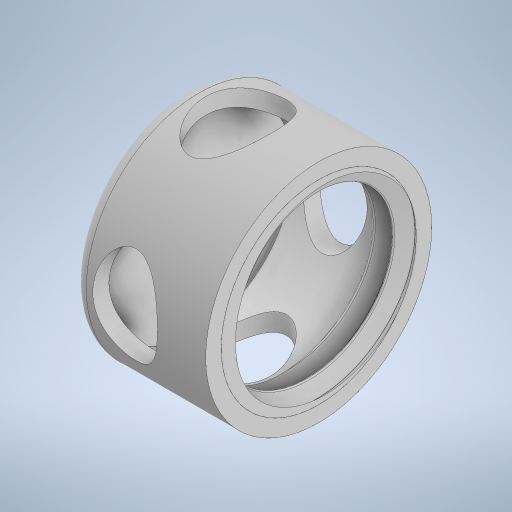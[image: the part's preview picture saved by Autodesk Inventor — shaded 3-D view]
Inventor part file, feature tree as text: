
AUTODESK INVENTOR PART (.ipt)
format: ipt  version: 2023 (Build 270158000, 158)  size: 494,080 bytes
history: native  units: in
note: dims shown in document units (in); Inventor stores cm internally (conversion verified against a paired STEP export)
features: sketch x6, extrude x5, fillet x1, thread x1, revolve x1, helix x1
ambient origin geometry x8: Origin, YZ Plane, XZ Plane, XY Plane, X Axis, Y Axis, Z Axis, Center Point
bodies: Solid1 (feature_tree), Solid11 (feature_tree)
feature tree (15):
  sketch  "Sketch1"  dims[d0=1.1811in d1=1.378in]
  extrude  "Extrusion2"  Depth=1.378in
  sketch  "Sketch2"  dims[d4=0.0591in d5=0.0in d6=0.1969in]
  sketch  "Sketch3"  dims[d7=0.2953in d8=0.315in]
  extrude  "Extrusion3"  Depth=0.1969in
  extrude  "Extrusion4"  Depth=0.315in
  extrude  "Extrusion5"  Depth=0.2953in
  fillet  "Fillet1"  Radius=0.315in
  extrude  "Extrusion7"  Depth=0.8071in TaperAngle=0.0deg
  thread  "Thread10"  [1 undecoded]
  revolve  "Revolution10"  [1 undecoded]
  helix  "Coil10"  [1 undecoded]
  sketch  "Sketch8"  dims[d9=0.1969in d10=0.2953in d11=0.315in]
  sketch  "Sketch23"  dims[d12=0.8071in d13=0.0in d14=1.5748in d15=0.0in d16=1.5748in d17=0.0in]
  sketch  "Sketch24"  dims[d27=0.3779in d38=0.0787in d48=0.3779in d59=1.189in d71=0.3779in d92=0.3779in d103=0.1969in d104=0.0in d114=0.3779in d134=0.3779in d154=0.3779in d176=0.3779in d196=0.3779in d207=0.1969in d208=0.0in d209=0.3779in d210=0.0189in d211=0.0189in d214=0.1232in d216=0.3779in d218=0.0in d219=0.1182in d220=0.4331in d221=0.3937in d222=0.0in d223=0.0in d224=0.0in d225=0.0in d226=0.0in]
note: 3 required parameter values undecoded (feature->parameter linkage not recoverable at this tier; creation-order binding heuristic only, values carry confidence <= 0.55)